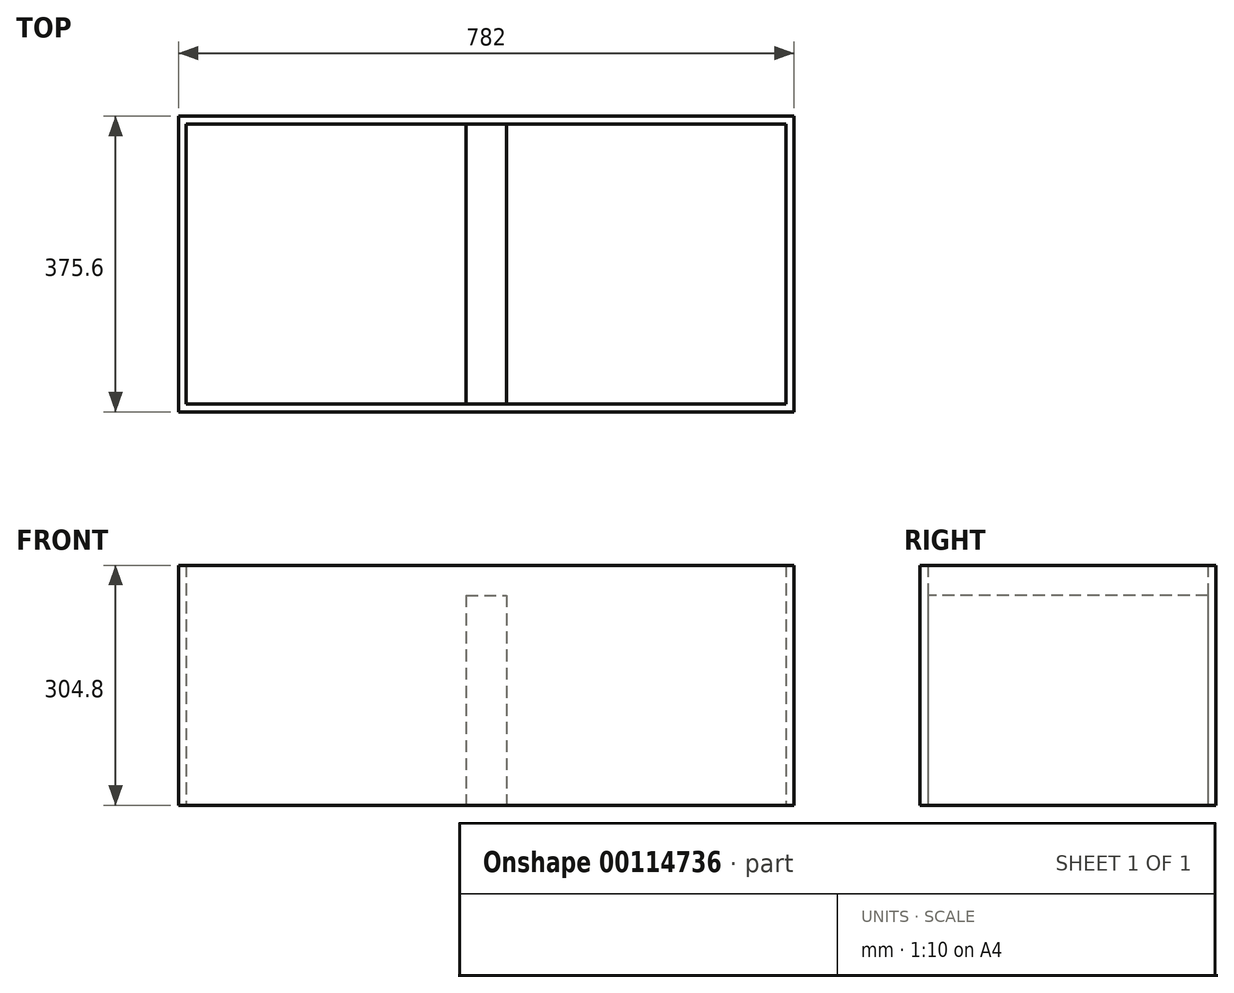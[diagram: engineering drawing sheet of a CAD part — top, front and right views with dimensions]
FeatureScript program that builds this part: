
annotation { "Feature Type Name" : "Feature", "Feature Type Description" : "" }
export const myFeature = defineFeature(function(context is Context, id is Id, definition is map)
    precondition{}
    {
        {
            var Q0;
            Q0=qCreatedBy(makeId("Top.planeOp"),FACE);
            var sketch = newSketch(context, id + "F0", { "sketchPlane" : qUnion([Q0])});
            skLineSegment(sketch, "E0.bottom", {"start": v(0, 0) * mm, "end": v(762, 0) * mm});
            skLineSegment(sketch, "E0.top", {"start": v(0, 355.6) * mm, "end": v(762, 355.6) * mm});
            skLineSegment(sketch, "E0.left", {"start": v(0, 0) * mm, "end": v(0, 355.6) * mm});
            skLineSegment(sketch, "E0.right", {"start": v(762, 0) * mm, "end": v(762, 355.6) * mm});
            skSolve(sketch);
        }
        {
            var Q0;
            Q0=qCreatedBy(makeId("Top.planeOp"),FACE);
            var sketch = newSketch(context, id + "F1", { "sketchPlane" : qUnion([Q0])});
            skLineSegment(sketch, "E1.bottom", {"start": v(-10, -10) * mm, "end": v(772, -10) * mm});
            skLineSegment(sketch, "E1.top", {"start": v(-10, 365.6) * mm, "end": v(772, 365.6) * mm});
            skLineSegment(sketch, "E1.left", {"start": v(-10, -10) * mm, "end": v(-10, 365.6) * mm});
            skLineSegment(sketch, "E1.right", {"start": v(772, -10) * mm, "end": v(772, 365.6) * mm});
            skSolve(sketch);
        }
        {
            var Q0;
            Q0 = qSketchRegion(id + "F1", true);
            extrude(context, id + "F2", {"entities" : qUnion([Q0]), "depth" : 304.8 * mm});
        }
        {
            var Q0;
            Q0 = qSketchRegion(id + "F0", true);
            extrude(context, id + "F3", {"entities" : qUnion([Q0]), "operationType" : NewBodyOperationType.REMOVE, "endBound" : BoundingType.THROUGH_ALL, "depth" : 25.4 * mm});
        }
        {
            var Q0;
            Q0=makeQuery(id+"F2.opExtrude","CAP_FACE",FACE,{"disambiguationData":[OSD([sQuery(id+"F1.wireOp",EDGE,"E1.bottom"),sQuery(id+"F1.wireOp",EDGE,"E1.top"),sQuery(id+"F1.wireOp",EDGE,"E1.left"),sQuery(id+"F1.wireOp",EDGE,"E1.right")])],"isStart":true});
            var sketch = newSketch(context, id + "F4", { "sketchPlane" : qUnion([Q0])});
            skLineSegment(sketch, "E2.bottom", {"start": v(355.6, -355.6) * mm, "end": v(406.4, -355.6) * mm});
            skLineSegment(sketch, "E2.top", {"start": v(355.6, 0) * mm, "end": v(406.4, 0) * mm});
            skLineSegment(sketch, "E2.left", {"start": v(355.6, -355.6) * mm, "end": v(355.6, 0) * mm});
            skLineSegment(sketch, "E2.right", {"start": v(406.4, -355.6) * mm, "end": v(406.4, 0) * mm});
            skPoint(sketch, "E3", {"position": v(381, -355.6) * mm});
            skSolve(sketch);
        }
        {
            var Q0;
            Q0 = qSketchRegion(id + "F4", true);
            extrude(context, id + "F5", {"entities" : qUnion([Q0]), "operationType" : NewBodyOperationType.ADD, "oppositeDirection" : true, "depth" : 266.7 * mm});
        }
    });
